# Revit family: Tub_Filler-DXV-Modulus-D35120951_Series
name_source: partatom
category: Plumbing Fixtures
units: mm (PartAtom-declared; Revit-internal decimal feet)

## family parameters
Always vertical = No
Cut with Voids When Loaded = Yes
OmniClass Number = 23.45.05.14.21
OmniClass Title = Bathtubs
Part Type = Normal
Room Calculation Point = No
Round Connector Dimension = Use Radius
Shared = Yes
Work Plane-Based = Yes

## types (4) — shared parameters
ASME A112.18.1/CSA B125.1 = Yes
Assembly Code = D2020300
CW Connection = Yes
CWFU = 3
Cold Water Connection Radius = 1/4"
Cold Water Diameter = 1/2"
Default Elevation = 0"
Description = DXV Modulus Floor Mount Tub Filler
Flow Rate = 1.8 gpm (6.8 L/min)
HW Connection = Yes
HWFU = 3
Height = 31 1/2"
Height Constrain = 32 1/2"
Hot Water Connection Diameter = 1/2"
Hot Water Connection Radius = 1/4"
Installation Instruction Link = https://dxv01.blob.core.windows.net
Installation Type = Wall Mounted
Length = 7 15/16"
Manufacturer = DXV
Price = Prices may vary. Please consult Manufacturer Rep for most up-to-date price list.
Product Documentation Link = https://dxv01.blob.core.windows.net
Product Page URL = https://www.dxv.com
Revised Date = 04/06/2022
URL = https://www.dxv.com
Vent Connection = No
WFU = 4
Waste Connection = No
Width = 2 9/16"

## per-type parameters (varying)
| type | Finish | Finish 2 | Height 2 | Material |
| D35120951.100 | Brass-DXV-100-Polished Chrome | Brass-DXV-144-Brushed Nickel | 0" | Brass-DXV-100-Polished Chrome |
| D35120951.144 | Brass-DXV-144-Brushed Nickel | Brass-DXV-144-Brushed Nickel | 0" | Brass-DXV-144-Brushed Nickel |
| D35120951.150 | Brass-DXV-150-Platinum Nickel | Brass-DXV-144-Brushed Nickel | 30" | Brass-DXV-150-Platinum Nickel |
| D35120951.243 | Brass-DXV-243-Matte Black | Brass-DXV-243-Matte Black | 0" | Brass-DXV-243-Matte Black |

note: column(s) folded — value = type name in every type: Model

## geometry (parser evidence)
native form markers: Sweep x4
no freeform markers — native parametric forms only
